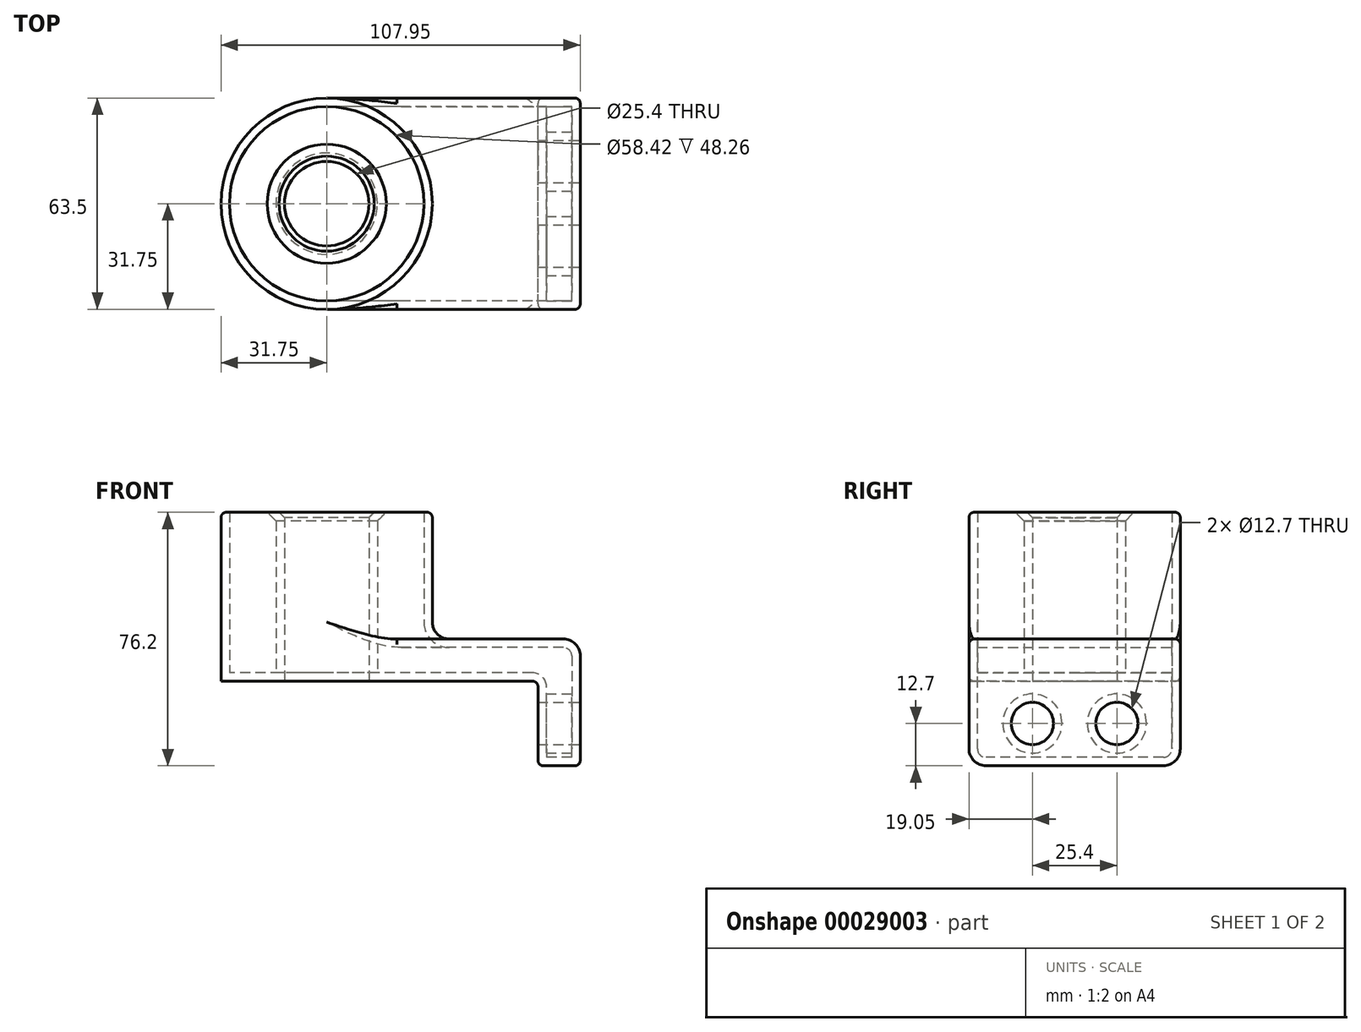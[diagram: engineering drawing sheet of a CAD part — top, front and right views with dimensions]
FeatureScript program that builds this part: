
annotation { "Feature Type Name" : "Feature", "Feature Type Description" : "" }
export const myFeature = defineFeature(function(context is Context, id is Id, definition is map)
    precondition{}
    {
        {
            var Q0;
            Q0=qCreatedBy(makeId("Top.planeOp"),FACE);
            var sketch = newSketch(context, id + "F0", { "sketchPlane" : qUnion([Q0])});
            skLineSegment(sketch, "E0.rect.bottom", {"start": v(38.1, 31.75) * mm, "end": v(-38.1, 31.75) * mm});
            skLineSegment(sketch, "E0.rect.top", {"start": v(38.1, -31.75) * mm, "end": v(-38.1, -31.75) * mm});
            skLineSegment(sketch, "E0.rect.left", {"start": v(38.1, 31.75) * mm, "end": v(38.1, -31.75) * mm});
            skLineSegment(sketch, "E0.rect.right", {"start": v(-38.1, 31.75) * mm, "end": v(-38.1, -31.75) * mm});
            skPoint(sketch, "E0.rect.middle", {"position": v(0, 0) * mm});
            skCircle(sketch, "E1", {"center": v(-38.1, 0) * mm, "radius": 31.75 * mm});
            skCircle(sketch, "E2", {"center": v(-38.1, 0) * mm, "radius": 12.7 * mm});
            skSolve(sketch);
        }
        {
            var Q0;
            Q0 = qSketchRegion(id + "F0", true);
            extrude(context, id + "F1", {"entities" : qUnion([Q0]), "depth" : 12.7 * mm});
        }
        {
            var Q0;
            {var subQ0=sQuery(id+"F0.wireOp",EDGE,"E2");var subQ1=sQuery(id+"F0.wireOp",EDGE,"E0.rect.right");var subQ3=makeQuery(id+"F0.imprint","INTERSECT",VERTEX,{"disambiguationData":[OD(0.0)],"derivedFrom":[subQ1,subQ0]});Q0=makeQuery(id+"F0.imprint","IMPRINT",FACE,{"disambiguationData":[TD([[makeQuery(id+"F0.imprint","IMPRINT",EDGE,{"disambiguationData":[TD([[subQ3,-1.0]])],"derivedFrom":subQ0}),-1.0]])]});}
            var Q1;
            {var subQ0=sQuery(id+"F0.wireOp",EDGE,"E2");var subQ1=sQuery(id+"F0.wireOp",EDGE,"E0.rect.right");var subQ3=makeQuery(id+"F0.imprint","INTERSECT",VERTEX,{"disambiguationData":[OD(0.0)],"derivedFrom":[subQ1,subQ0]});Q1=makeQuery(id+"F0.imprint","IMPRINT",FACE,{"disambiguationData":[TD([[makeQuery(id+"F0.imprint","IMPRINT",EDGE,{"disambiguationData":[TD([[subQ3,1.0]])],"derivedFrom":subQ0}),-1.0]])]});}
            extrude(context, id + "F2", {"entities" : qUnion([Q0, Q1]), "operationType" : NewBodyOperationType.ADD, "depth" : 50.8 * mm});
        }
        {
            var Q0;
            Q0=makeQuery(id+"F1.opExtrude","SWEPT_FACE",FACE,{"disambiguationData":[OSD([sQuery(id+"F0.wireOp",EDGE,"E0.rect.left")])]});
            var sketch = newSketch(context, id + "F3", { "sketchPlane" : qUnion([Q0])});
            skLineSegment(sketch, "E3.bottom", {"start": v(-31.75, 12.7) * mm, "end": v(31.75, 12.7) * mm});
            skLineSegment(sketch, "E3.top", {"start": v(-31.75, -25.4) * mm, "end": v(31.75, -25.4) * mm});
            skLineSegment(sketch, "E3.left", {"start": v(-31.75, 12.7) * mm, "end": v(-31.75, -25.4) * mm});
            skLineSegment(sketch, "E3.right", {"start": v(31.75, 12.7) * mm, "end": v(31.75, -25.4) * mm});
            skCircle(sketch, "E4", {"center": v(-12.7, -12.7) * mm, "radius": 6.35 * mm});
            skLineSegment(sketch, "E5", {"start": v(0, 0) * mm, "end": v(0, -25.4) * mm, "construction": true});
            skCircle(sketch, "E6.MirrorC", {"center": v(12.7, -12.7) * mm, "radius": 6.35 * mm});
            skSolve(sketch);
        }
        {
            var Q0;
            Q0 = qSketchRegion(id + "F3", true);
            extrude(context, id + "F4", {"entities" : qUnion([Q0]), "operationType" : NewBodyOperationType.ADD, "oppositeDirection" : true, "depth" : 12.7 * mm});
        }
        {
            var Q0;
            {var subQ0=sQuery(id+"F0.wireOp",EDGE,"E1");Q0=makeQuery(id+"F2.boolean.opBoolean","INTERSECT",EDGE,{"derivedFrom":[makeQuery(id+"F1.opExtrude","CAP_FACE",FACE,{"disambiguationData":[OSD([sQuery(id+"F0.wireOp",EDGE,"E0.rect.bottom"),sQuery(id+"F0.wireOp",EDGE,"E0.rect.top"),sQuery(id+"F0.wireOp",EDGE,"E0.rect.left"),subQ0,sQuery(id+"F0.wireOp",EDGE,"E2")])],"isStart":false}),makeQuery(id+"F2.opExtrude","SWEPT_FACE",FACE,{"disambiguationData":[OSD([subQ0])]})]});}
            var Q1;
            Q1=makeQuery(id+"F1.opExtrude","CAP_EDGE",EDGE,{"disambiguationData":[OSD([sQuery(id+"F0.wireOp",EDGE,"E0.rect.left")])],"isStart":false});
            var Q2;
            Q2=makeQuery(id+"F4.opExtrude","SWEPT_EDGE",EDGE,{"disambiguationData":[OSD([sQuery(id+"F3.wireOp",EDGE,"E3.top"),sQuery(id+"F3.wireOp",EDGE,"E3.left")])]});
            var Q3;
            Q3=makeQuery(id+"F4.opExtrude","SWEPT_EDGE",EDGE,{"disambiguationData":[OSD([sQuery(id+"F3.wireOp",EDGE,"E3.top"),sQuery(id+"F3.wireOp",EDGE,"E3.right")])]});
            fillet(context, id + "F5", {"entities" : qUnion([Q0, Q1, Q2, Q3]), "radius" : 5.08 * mm, "tangentPropagation" : true, "allowEdgeOverflow" : false});
        }
        {
            var Q0;
            Q0=makeQuery(id+"F1.opExtrude","CAP_EDGE",EDGE,{"disambiguationData":[OSD([sQuery(id+"F0.wireOp",EDGE,"E0.rect.top")])],"isStart":false});
            var Q1;
            Q1=makeQuery(id+"F4.boolean.opBoolean","INTERSECT",EDGE,{"derivedFrom":[makeQuery(id+"F1.opExtrude","CAP_FACE",FACE,{"disambiguationData":[OSD([sQuery(id+"F0.wireOp",EDGE,"E0.rect.bottom"),sQuery(id+"F0.wireOp",EDGE,"E0.rect.top"),sQuery(id+"F0.wireOp",EDGE,"E0.rect.left"),sQuery(id+"F0.wireOp",EDGE,"E1"),sQuery(id+"F0.wireOp",EDGE,"E2")])],"isStart":true}),makeQuery(id+"F4.opExtrude","CAP_FACE",FACE,{"disambiguationData":[OSD([sQuery(id+"F3.wireOp",EDGE,"E3.bottom"),sQuery(id+"F3.wireOp",EDGE,"E3.top"),sQuery(id+"F3.wireOp",EDGE,"E3.left"),sQuery(id+"F3.wireOp",EDGE,"E3.right"),sQuery(id+"F3.wireOp",EDGE,"E4"),sQuery(id+"F3.wireOp",EDGE,"E6.MirrorC")])],"isStart":false})]});
            var Q2;
            Q2=makeQuery(id+"F4.opExtrude","CAP_EDGE",EDGE,{"disambiguationData":[OSD([sQuery(id+"F3.wireOp",EDGE,"E3.left")])],"isStart":false});
            fillet(context, id + "F6", {"entities" : qUnion([Q0, Q1, Q2]), "radius" : 1.6 * mm, "tangentPropagation" : true, "allowEdgeOverflow" : false});
        }
        {
            var Q0;
            Q0=makeQuery(id+"F2.opExtrude","CAP_EDGE",EDGE,{"disambiguationData":[OSD([sQuery(id+"F0.wireOp",EDGE,"E2")])],"isStart":false});
            chamfer(context, id + "F7", {"entities" : qUnion([Q0]), "width" : 1.6 * mm, "tangentPropagation" : true});
        }
        {
            var Q0;
            Q0=makeQuery(id+"F2.opExtrude","CAP_EDGE",EDGE,{"disambiguationData":[OSD([sQuery(id+"F0.wireOp",EDGE,"E1")])],"isStart":false});
            fillet(context, id + "F8", {"entities" : qUnion([Q0]), "radius" : 1.6 * mm, "tangentPropagation" : true, "allowEdgeOverflow" : false});
        }
        {
            var Q0;
            Q0=makeQuery(id+"F2.opExtrude","CAP_FACE",FACE,{"disambiguationData":[OSD([sQuery(id+"F0.wireOp",EDGE,"E1"),sQuery(id+"F0.wireOp",EDGE,"E2")])],"isStart":false});
            shell(context, id + "F9", {"entities" : qUnion([Q0]), "thickness" : 2.54 * mm});
        }
    });
